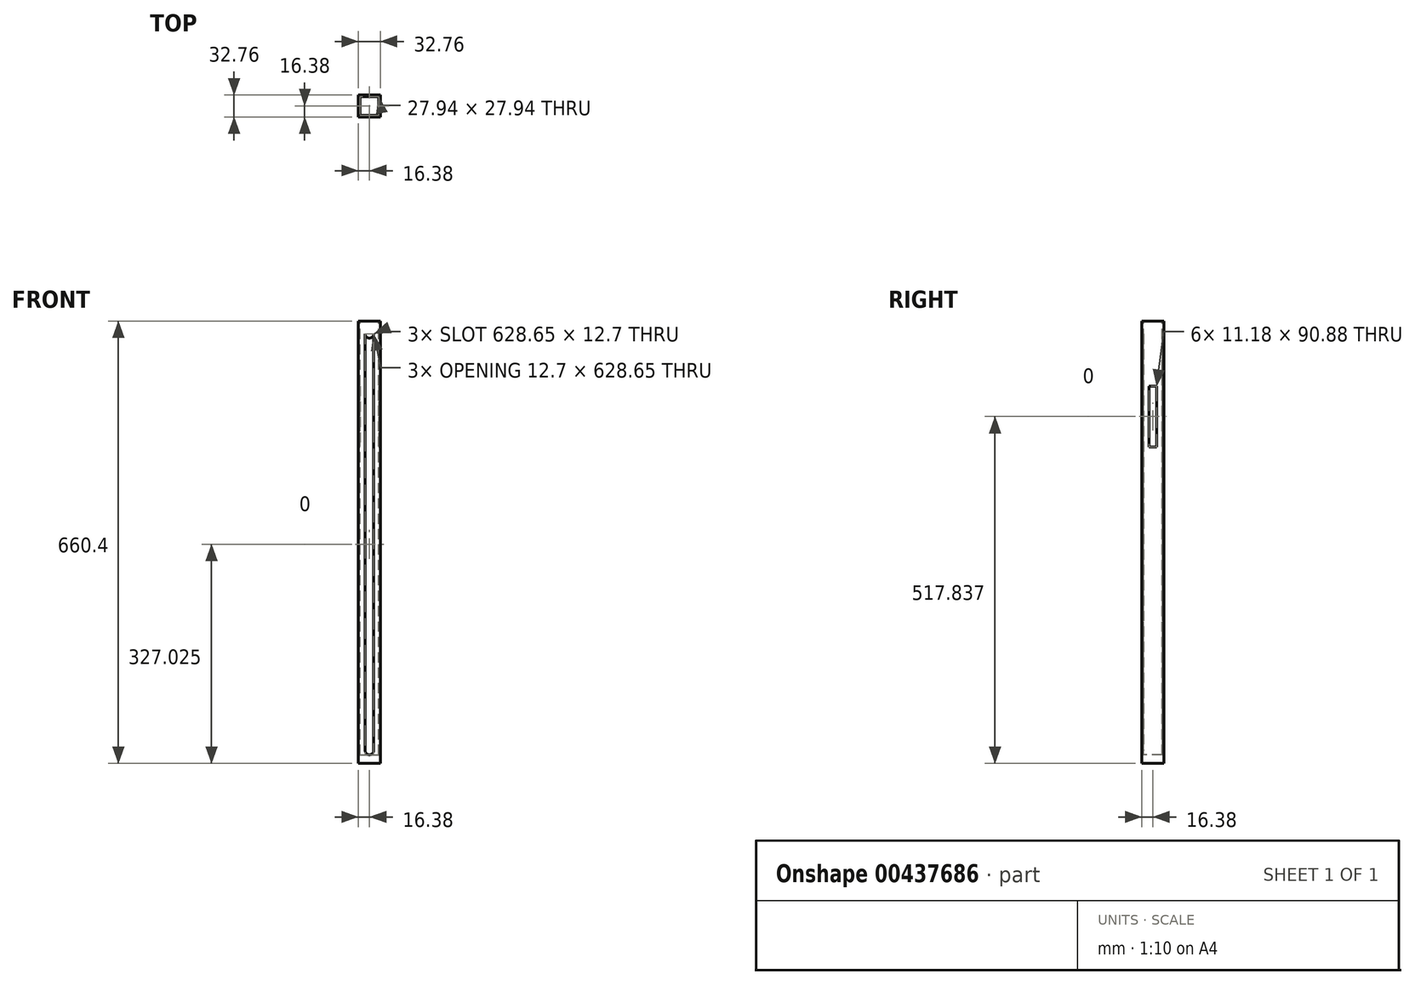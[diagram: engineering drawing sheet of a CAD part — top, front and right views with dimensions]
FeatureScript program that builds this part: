
annotation { "Feature Type Name" : "Feature", "Feature Type Description" : "" }
export const myFeature = defineFeature(function(context is Context, id is Id, definition is map)
    precondition{}
    {
        {
            var Q0;
            Q0=qCreatedBy(makeId("Top.planeOp"),FACE);
            var sketch = newSketch(context, id + "F0", { "sketchPlane" : qUnion([Q0])});
            skLineSegment(sketch, "E0.bottom", {"start": v(-16.38, 16.38) * mm, "end": v(16.38, 16.38) * mm});
            skLineSegment(sketch, "E0.top", {"start": v(-16.38, -16.38) * mm, "end": v(16.38, -16.38) * mm});
            skLineSegment(sketch, "E0.left", {"start": v(-16.38, 16.38) * mm, "end": v(-16.38, -16.38) * mm});
            skLineSegment(sketch, "E0.right", {"start": v(16.38, 16.38) * mm, "end": v(16.38, -16.38) * mm});
            skPoint(sketch, "E0.middle", {"position": v(0, 0) * mm});
            skSolve(sketch);
        }
        {
            var Q0;
            Q0=makeQuery(id+"F0.imprint","IMPRINT",FACE,{"disambiguationData":[TD([[makeQuery(id+"F0.imprint","IMPRINT",EDGE,{"derivedFrom":sQuery(id+"F0.wireOp",EDGE,"E0.bottom")}),-1.0]])]});
            extrude(context, id + "F1", {"entities" : qUnion([Q0]), "depth" : 660.4 * mm});
        }
        {
            var Q0;
            Q0=makeQuery(id+"F1.opExtrude","CAP_FACE",FACE,{"disambiguationData":[OSD([sQuery(id+"F0.wireOp",EDGE,"E0.bottom"),sQuery(id+"F0.wireOp",EDGE,"E0.top"),sQuery(id+"F0.wireOp",EDGE,"E0.left"),sQuery(id+"F0.wireOp",EDGE,"E0.right")])],"isStart":false});
            var sketch = newSketch(context, id + "F2", { "sketchPlane" : qUnion([Q0])});
            skLineSegment(sketch, "E1", {"start": v(0, 16.38) * mm, "end": v(0, -16.38) * mm});
            skLineSegment(sketch, "E2", {"start": v(-16.38, 0) * mm, "end": v(16.38, 0) * mm});
            skLineSegment(sketch, "E3.bottom", {"start": v(-13.97, 13.97) * mm, "end": v(13.97, 13.97) * mm});
            skLineSegment(sketch, "E3.top", {"start": v(-13.97, -13.97) * mm, "end": v(13.97, -13.97) * mm});
            skLineSegment(sketch, "E3.left", {"start": v(-13.97, 13.97) * mm, "end": v(-13.97, -13.97) * mm});
            skLineSegment(sketch, "E3.right", {"start": v(13.97, 13.97) * mm, "end": v(13.97, -13.97) * mm});
            skPoint(sketch, "E3.middle", {"position": v(0, 0) * mm});
            skSolve(sketch);
        }
        {
            var Q0;
            {var subQ0=sQuery(id+"F2.wireOp",EDGE,"E3.bottom");var subQ1=sQuery(id+"F2.wireOp",EDGE,"E1");var subQ2=makeQuery(id+"F2.imprint","INTERSECT",VERTEX,{"derivedFrom":[subQ1,subQ0]});Q0=makeQuery(id+"F2.imprint","IMPRINT",FACE,{"disambiguationData":[TD([[makeQuery(id+"F2.imprint","IMPRINT",EDGE,{"disambiguationData":[TD([[subQ2,-1.0]])],"derivedFrom":subQ1}),-1.0]])]});}
            var Q1;
            {var subQ0=sQuery(id+"F2.wireOp",EDGE,"E3.bottom");var subQ1=sQuery(id+"F2.wireOp",EDGE,"E1");var subQ2=makeQuery(id+"F2.imprint","INTERSECT",VERTEX,{"derivedFrom":[subQ1,subQ0]});Q1=makeQuery(id+"F2.imprint","IMPRINT",FACE,{"disambiguationData":[TD([[makeQuery(id+"F2.imprint","IMPRINT",EDGE,{"disambiguationData":[TD([[subQ2,-1.0]])],"derivedFrom":subQ1}),1.0]])]});}
            var Q2;
            {var subQ0=sQuery(id+"F2.wireOp",EDGE,"E2");var subQ1=sQuery(id+"F2.wireOp",EDGE,"E1");var subQ2=makeQuery(id+"F2.imprint","INTERSECT",VERTEX,{"derivedFrom":[subQ1,subQ0]});Q2=makeQuery(id+"F2.imprint","IMPRINT",FACE,{"disambiguationData":[TD([[makeQuery(id+"F2.imprint","IMPRINT",EDGE,{"disambiguationData":[TD([[subQ2,-1.0]])],"derivedFrom":subQ1}),1.0]])]});}
            var Q3;
            {var subQ0=sQuery(id+"F2.wireOp",EDGE,"E2");var subQ1=sQuery(id+"F2.wireOp",EDGE,"E1");var subQ2=makeQuery(id+"F2.imprint","INTERSECT",VERTEX,{"derivedFrom":[subQ1,subQ0]});Q3=makeQuery(id+"F2.imprint","IMPRINT",FACE,{"disambiguationData":[TD([[makeQuery(id+"F2.imprint","IMPRINT",EDGE,{"disambiguationData":[TD([[subQ2,-1.0]])],"derivedFrom":subQ1}),-1.0]])]});}
            extrude(context, id + "F3", {"entities" : qUnion([Q0, Q1, Q2, Q3]), "operationType" : NewBodyOperationType.REMOVE, "oppositeDirection" : true, "depth" : 647.7 * mm});
        }
        {
            var Q0;
            Q0=makeQuery(id+"F1.opExtrude","SWEPT_FACE",FACE,{"disambiguationData":[OSD([sQuery(id+"F0.wireOp",EDGE,"E0.top")])]});
            var sketch = newSketch(context, id + "F4", { "sketchPlane" : qUnion([Q0])});
            skLineSegment(sketch, "E4", {"start": v(0, 660.4) * mm, "end": v(0, 0) * mm});
            skCircle(sketch, "E5", {"center": v(0, 641.35) * mm, "radius": 6.35 * mm});
            skCircle(sketch, "E6", {"center": v(0, 19.05) * mm, "radius": 6.35 * mm});
            skLineSegment(sketch, "E7", {"start": v(-6.35, 641.35) * mm, "end": v(-6.35, 19.05) * mm});
            skLineSegment(sketch, "E8", {"start": v(6.35, 641.35) * mm, "end": v(6.35, 19.05) * mm});
            skSolve(sketch);
        }
        {
            var Q0;
            {var subQ5=sQuery(id+"F4.wireOp",EDGE,"E7");Q0=makeQuery(id+"F4.imprint","IMPRINT",FACE,{"disambiguationData":[TD([[makeQuery(id+"F4.imprint","IMPRINT",EDGE,{"derivedFrom":subQ5}),1.0]])]});}
            var Q1;
            {var subQ0=sQuery(id+"F4.wireOp",EDGE,"E5");var subQ1=sQuery(id+"F4.wireOp",EDGE,"E4");var subQ2=makeQuery(id+"F4.imprint","INTERSECT",VERTEX,{"disambiguationData":[OD(0.0)],"derivedFrom":[subQ1,subQ0]});Q1=makeQuery(id+"F4.imprint","IMPRINT",FACE,{"disambiguationData":[TD([[makeQuery(id+"F4.imprint","IMPRINT",EDGE,{"disambiguationData":[TD([[subQ2,-1.0]])],"derivedFrom":subQ1}),-1.0]])]});}
            var Q2;
            {var subQ0=sQuery(id+"F4.wireOp",EDGE,"E5");var subQ1=sQuery(id+"F4.wireOp",EDGE,"E4");var subQ2=makeQuery(id+"F4.imprint","INTERSECT",VERTEX,{"disambiguationData":[OD(0.0)],"derivedFrom":[subQ1,subQ0]});Q2=makeQuery(id+"F4.imprint","IMPRINT",FACE,{"disambiguationData":[TD([[makeQuery(id+"F4.imprint","IMPRINT",EDGE,{"disambiguationData":[TD([[subQ2,-1.0]])],"derivedFrom":subQ1}),1.0]])]});}
            var Q3;
            {var subQ5=sQuery(id+"F4.wireOp",EDGE,"E8");Q3=makeQuery(id+"F4.imprint","IMPRINT",FACE,{"disambiguationData":[TD([[makeQuery(id+"F4.imprint","IMPRINT",EDGE,{"derivedFrom":subQ5}),-1.0]])]});}
            var Q4;
            {var subQ0=sQuery(id+"F4.wireOp",EDGE,"E6");var subQ1=sQuery(id+"F4.wireOp",EDGE,"E4");var subQ2=makeQuery(id+"F4.imprint","INTERSECT",VERTEX,{"disambiguationData":[OD(0.0)],"derivedFrom":[subQ1,subQ0]});Q4=makeQuery(id+"F4.imprint","IMPRINT",FACE,{"disambiguationData":[TD([[makeQuery(id+"F4.imprint","IMPRINT",EDGE,{"disambiguationData":[TD([[subQ2,-1.0]])],"derivedFrom":subQ1}),-1.0]])]});}
            var Q5;
            {var subQ0=sQuery(id+"F4.wireOp",EDGE,"E6");var subQ1=sQuery(id+"F4.wireOp",EDGE,"E4");var subQ2=makeQuery(id+"F4.imprint","INTERSECT",VERTEX,{"disambiguationData":[OD(0.0)],"derivedFrom":[subQ1,subQ0]});Q5=makeQuery(id+"F4.imprint","IMPRINT",FACE,{"disambiguationData":[TD([[makeQuery(id+"F4.imprint","IMPRINT",EDGE,{"disambiguationData":[TD([[subQ2,-1.0]])],"derivedFrom":subQ1}),1.0]])]});}
            extrude(context, id + "F5", {"entities" : qUnion([Q0, Q1, Q2, Q3, Q4, Q5]), "operationType" : NewBodyOperationType.REMOVE, "oppositeDirection" : true, "depth" : 66.3 * mm});
        }
        {
            var Q0;
            Q0=makeQuery(id+"F1.opExtrude","SWEPT_FACE",FACE,{"disambiguationData":[OSD([sQuery(id+"F0.wireOp",EDGE,"E0.right")])]});
            var sketch = newSketch(context, id + "F6", { "sketchPlane" : qUnion([Q0])});
            skLineSegment(sketch, "E9.bottom", {"start": v(5.6, 472.4) * mm, "end": v(-5.6, 472.4) * mm});
            skLineSegment(sketch, "E9.top", {"start": v(5.6, 848.4) * mm, "end": v(-5.6, 848.4) * mm});
            skLineSegment(sketch, "E9.left", {"start": v(5.6, 472.4) * mm, "end": v(5.6, 848.4) * mm});
            skLineSegment(sketch, "E9.right", {"start": v(-5.6, 472.4) * mm, "end": v(-5.6, 848.4) * mm});
            skPoint(sketch, "E9.middle", {"position": v(0, 660.4) * mm});
            skLineSegment(sketch, "E10", {"start": v(-5.6, 563.28) * mm, "end": v(5.6, 563.28) * mm});
            skSolve(sketch);
        }
        {
            var Q0;
            {var subQ0=sQuery(id+"F6.wireOp",EDGE,"E9.bottom");Q0=makeQuery(id+"F6.imprint","IMPRINT",FACE,{"disambiguationData":[TD([[makeQuery(id+"F6.imprint","IMPRINT",EDGE,{"derivedFrom":subQ0}),-1.0]])]});}
            extrude(context, id + "F7", {"entities" : qUnion([Q0]), "operationType" : NewBodyOperationType.REMOVE, "oppositeDirection" : true, "depth" : 96.27 * mm});
        }
    });
